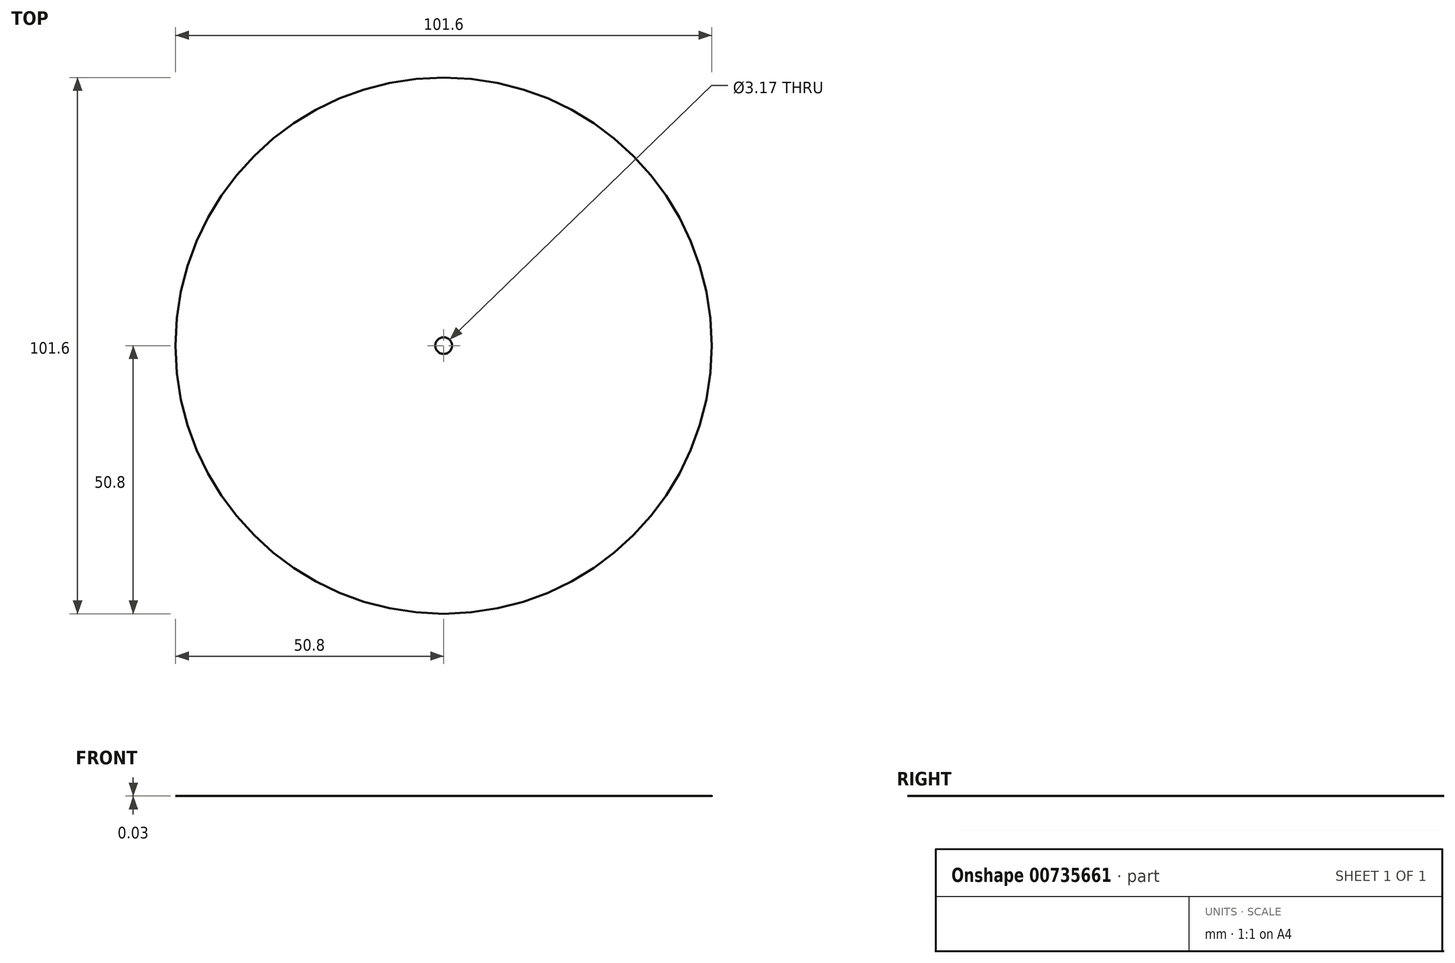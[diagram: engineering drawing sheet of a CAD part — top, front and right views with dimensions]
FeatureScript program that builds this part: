
annotation { "Feature Type Name" : "Feature", "Feature Type Description" : "" }
export const myFeature = defineFeature(function(context is Context, id is Id, definition is map)
    precondition{}
    {
        {
            var Q0;
            Q0=qCreatedBy(makeId("Top.planeOp"),FACE);
            var sketch = newSketch(context, id + "F0", { "sketchPlane" : qUnion([Q0])});
            skCircle(sketch, "E0", {"center": v(0, 0) * mm, "radius": 50.8 * mm});
            skCircle(sketch, "E1", {"center": v(0, 0) * mm, "radius": 1.59 * mm});
            skSolve(sketch);
        }
        {
            var Q0;
            Q0 = qSketchRegion(id + "F0", true);
            extrude(context, id + "F1", {"entities" : qUnion([Q0]), "depth" : 7 / 203.2 * mm, "offsetDistance" : 25.4 * mm});
        }
    });
